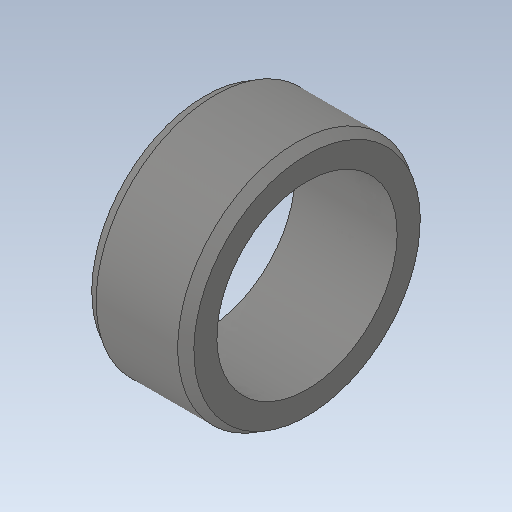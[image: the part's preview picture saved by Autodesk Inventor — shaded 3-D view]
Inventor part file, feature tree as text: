
AUTODESK INVENTOR PART (.ipt)
format: ipt  version: 2020 (Build 240168000, 168)  size: 130,560 bytes
history: native  units: mm
features: other x21, revolve x1, sketch x1
ambient origin geometry x8: Origin, YZ Plane, XZ Plane, XY Plane, X Axis, Y Axis, Z Axis, Center Point
bodies: Solid1 (feature_tree)
feature tree (23):
  revolve  "Revolution1"  [1 undecoded]
  other  "anbau_XY"
  other  "anbau_YZ"
  other  "anbau_ZX"
  other  "anbau_X"
  other  "anbau_Y"
  other  "anbau_Z"
  other  "anbau_Center"
  other  "insert_XY"
  other  "insert_YZ"
  other  "insert_ZX"
  other  "insert_X"
  other  "insert_Y"
  other  "insert_Z"
  other  "insert_Center"
  other  "schraube_punkt_XY"
  other  "schraube_punkt_YZ"
  other  "schraube_punkt_ZX"
  other  "schraube_punkt_X"
  other  "schraube_punkt_Y"
  other  "schraube_punkt_Z"
  other  "schraube_punkt_Center"
  sketch  "Sketch_1"  dims[d0=360.0deg d1=0.0mm d2=0.0mm d3=0.0mm]
note: 1 required parameter value undecoded (feature->parameter linkage not recoverable at this tier; creation-order binding heuristic only, values carry confidence <= 0.55)
